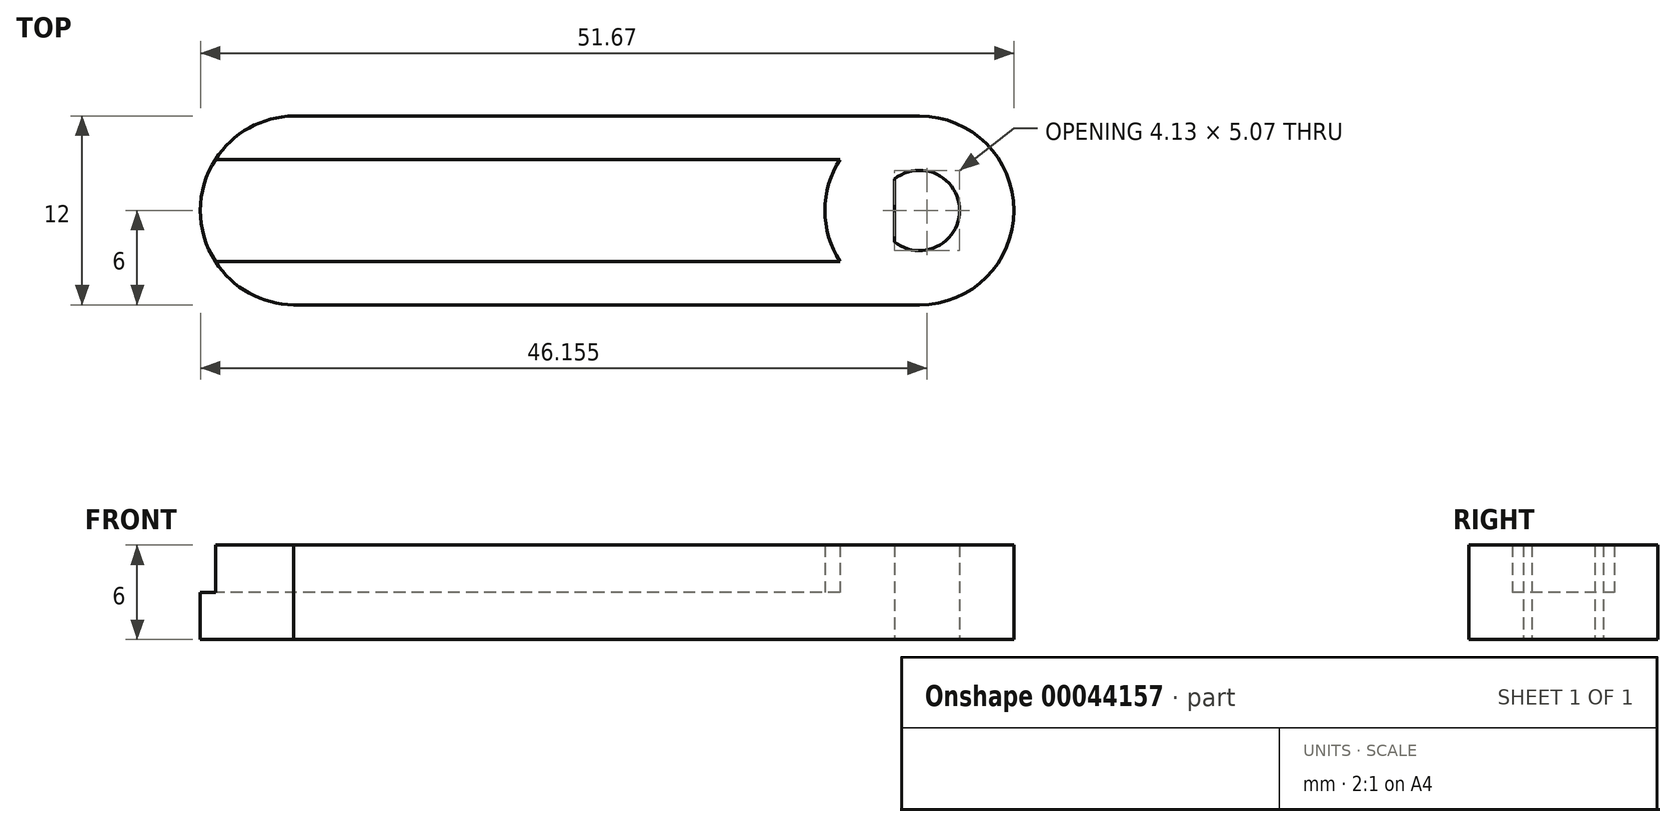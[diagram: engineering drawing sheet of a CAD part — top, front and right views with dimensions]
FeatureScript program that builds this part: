
annotation { "Feature Type Name" : "Feature", "Feature Type Description" : "" }
export const myFeature = defineFeature(function(context is Context, id is Id, definition is map)
    precondition{}
    {
        {
            var Q0;
            Q0=qCreatedBy(makeId("Top.planeOp"),FACE);
            var sketch = newSketch(context, id + "F0", { "sketchPlane" : qUnion([Q0])});
            skCircle(sketch, "E0", {"center": v(-0.08, 0) * mm, "radius": 2.55 * mm});
            skLineSegment(sketch, "E1", {"start": v(-1.66, 2) * mm, "end": v(-1.66, -2) * mm});
            skArc(sketch, "E2", {"start": v(-5.12, 3.25) * mm, "mid": v(-6.08, 0) * mm, "end": v(-5.12, -3.25) * mm});
            skLineSegment(sketch, "E3.MirrorCS", {"start": v(-0.08, -6) * mm, "end": v(-39.83, -6) * mm});
            skArc(sketch, "E4", {"start": v(-39.75, 6) * mm, "mid": v(-45.75, 0.04) * mm, "end": v(-39.83, -6) * mm});
            skPoint(sketch, "E5.orphan", {"position": v(-0.08, 6) * mm});
            skLineSegment(sketch, "E6.MirrorCS", {"start": v(-0.08, 6) * mm, "end": v(-39.83, 6) * mm});
            skLineSegment(sketch, "E7", {"start": v(-5.12, 3.25) * mm, "end": v(-44.8, 3.25) * mm});
            skLineSegment(sketch, "E8.MirrorCS", {"start": v(-5.12, -3.25) * mm, "end": v(-44.8, -3.25) * mm});
            skArc(sketch, "E9.trimOffspring", {"start": v(-0.08, -6) * mm, "mid": v(5.92, 0) * mm, "end": v(-0.08, 6) * mm});
            skSolve(sketch);
        }
        {
            var Q0;
            {var subQ0=sQuery(id+"F0.wireOp",EDGE,"E1");Q0=makeQuery(id+"F0.imprint","IMPRINT",FACE,{"disambiguationData":[TD([[makeQuery(id+"F0.imprint","IMPRINT",EDGE,{"derivedFrom":subQ0}),-1.0]])]});}
            var Q1;
            {var subQ0=sQuery(id+"F0.wireOp",EDGE,"E1");var subQ1=sQuery(id+"F0.wireOp",EDGE,"E0");var subQ2=makeQuery(id+"F0.imprint","INTERSECT",VERTEX,{"disambiguationData":[OD(0.0)],"derivedFrom":[subQ1,subQ0]});Q1=makeQuery(id+"F0.imprint","IMPRINT",FACE,{"disambiguationData":[TD([[makeQuery(id+"F0.imprint","IMPRINT",EDGE,{"disambiguationData":[TD([[subQ2,-1.0]])],"derivedFrom":subQ1}),-1.0]])]});}
            extrude(context, id + "F1", {"entities" : qUnion([Q0, Q1]), "depth" : 6 * mm, "offsetDistance" : 25 * mm});
        }
        {
            var Q0;
            Q0=makeQuery(id+"F0.imprint","IMPRINT",FACE,{"disambiguationData":[TD([[makeQuery(id+"F0.imprint","IMPRINT",EDGE,{"derivedFrom":sQuery(id+"F0.wireOp",EDGE,"E2")}),-1.0]])]});
            extrude(context, id + "F2", {"entities" : qUnion([Q0]), "operationType" : NewBodyOperationType.ADD, "depth" : 3 * mm, "offsetDistance" : 25 * mm});
        }
    });
